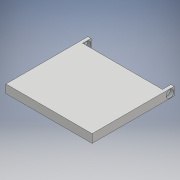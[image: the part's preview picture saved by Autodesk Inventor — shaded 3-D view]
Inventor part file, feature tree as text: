
AUTODESK INVENTOR PART (.ipt)
format: ipt  version: 2018 (Build 220112000, 112)  size: 123,904 bytes
history: native  units: mm
features: extrude x4, sketch x4, projected_geometry x4
ambient origin geometry x8: Origin, YZ Plane, XZ Plane, XY Plane, X Axis, Y Axis, Z Axis, Center Point
bodies: Solid1 (feature_tree)
feature tree (12):
  extrude  "Extrusion1"  Depth=700.0mm
  extrude  "Extrusion2"  Depth=80.0mm
  extrude  "Extrusion3"  Depth=30.0mm TaperAngle=0.0deg
  extrude  "Extrusion4"  Depth=30.0mm
  sketch  "Sketch1"  dims[d0=820.0mm d1=700.0mm]
  sketch  "Sketch2"  dims[d2=80.0mm d3=0.0mm d4=80.0mm]
  projected_geometry  "Projected Loop1"
  sketch  "Sketch3"  dims[d5=80.0mm d6=30.0mm d7=0.0mm]
  projected_geometry  "Projected Loop2"
  projected_geometry  "Projected Loop3"
  sketch  "Sketch4"  dims[d8=30.0mm d9=0.0mm d10=73.0mm d11=940.75mm d12=0.0mm]
  projected_geometry  "Projected Loop4"
